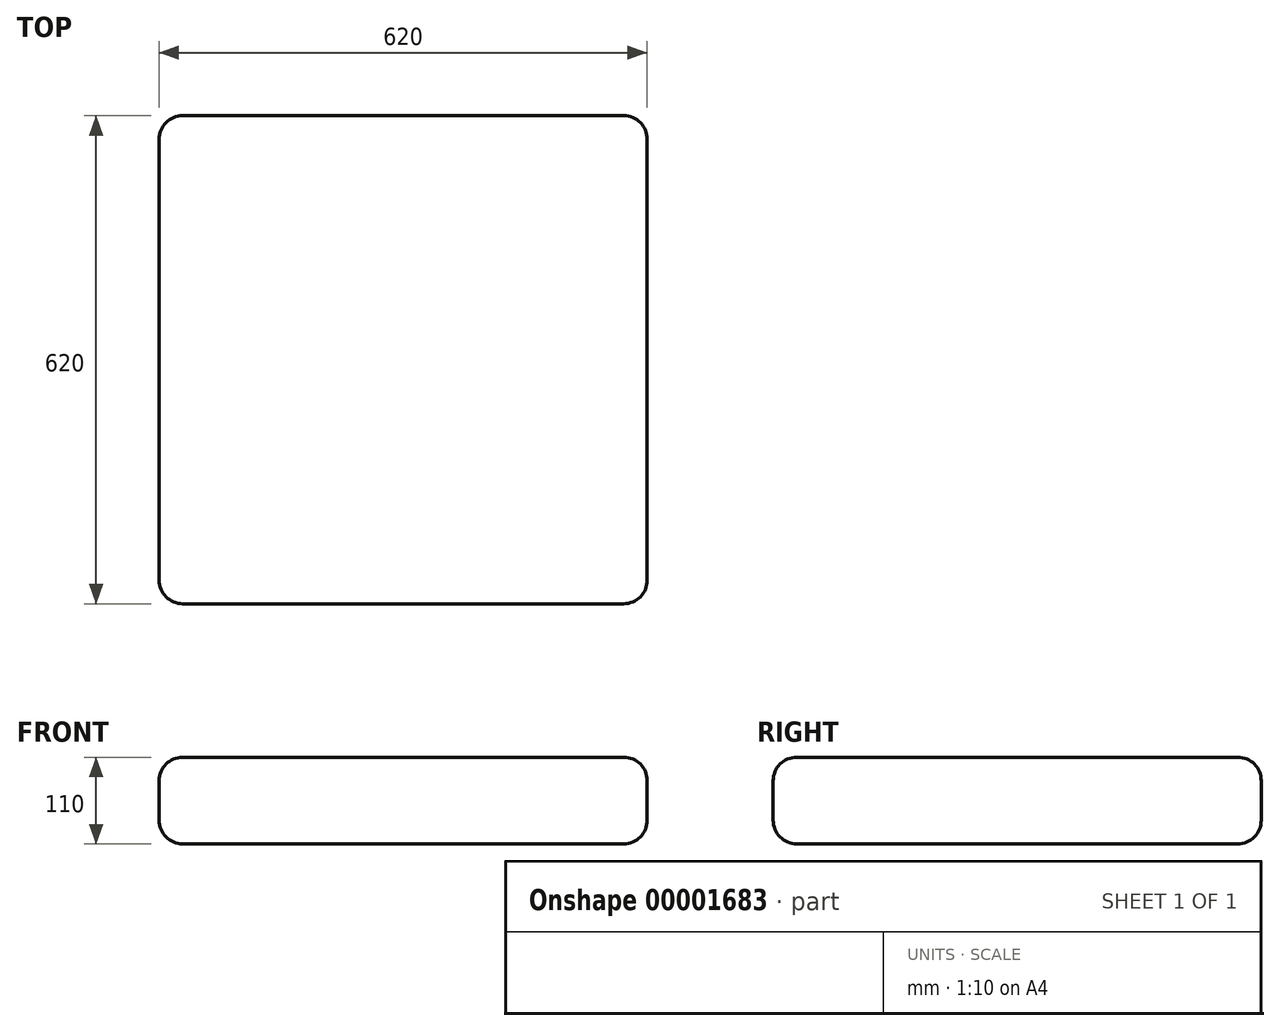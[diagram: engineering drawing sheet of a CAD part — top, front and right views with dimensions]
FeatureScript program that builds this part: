
annotation { "Feature Type Name" : "Feature", "Feature Type Description" : "" }
export const myFeature = defineFeature(function(context is Context, id is Id, definition is map)
    precondition{}
    {
        {
            var Q0;
            Q0=qCreatedBy(makeId("Top.planeOp"),FACE);
            var sketch = newSketch(context, id + "F0", { "sketchPlane" : qUnion([Q0])});
            skLineSegment(sketch, "E0.bottom", {"start": v(0, 0) * mm, "end": v(620, 0) * mm});
            skLineSegment(sketch, "E0.top", {"start": v(0, 620) * mm, "end": v(620, 620) * mm});
            skLineSegment(sketch, "E0.left", {"start": v(0, 0) * mm, "end": v(0, 620) * mm});
            skLineSegment(sketch, "E0.right", {"start": v(620, 0) * mm, "end": v(620, 620) * mm});
            skSolve(sketch);
        }
        {
            var Q0;
            Q0=makeQuery(id+"F0.imprint","IMPRINT",FACE,{"disambiguationData":[TD([[makeQuery(id+"F0.imprint","IMPRINT",EDGE,{"derivedFrom":sQuery(id+"F0.wireOp",EDGE,"E0.bottom")}),1.0]])]});
            extrude(context, id + "F1", {"entities" : qUnion([Q0]), "depth" : 110 * mm});
        }
        {
            var Q0;
            Q0=makeQuery(id+"F1.opExtrude","CAP_EDGE",EDGE,{"disambiguationData":[OSD([sQuery(id+"F0.wireOp",EDGE,"E0.bottom")])],"isStart":false});
            var Q1;
            Q1=makeQuery(id+"F1.opExtrude","CAP_EDGE",EDGE,{"disambiguationData":[OSD([sQuery(id+"F0.wireOp",EDGE,"E0.right")])],"isStart":false});
            var Q2;
            Q2=makeQuery(id+"F1.opExtrude","SWEPT_EDGE",EDGE,{"disambiguationData":[OSD([sQuery(id+"F0.wireOp",EDGE,"E0.bottom"),sQuery(id+"F0.wireOp",EDGE,"E0.right")])]});
            var Q3;
            Q3=makeQuery(id+"F1.opExtrude","SWEPT_EDGE",EDGE,{"disambiguationData":[OSD([sQuery(id+"F0.wireOp",EDGE,"E0.top"),sQuery(id+"F0.wireOp",EDGE,"E0.right")])]});
            var Q4;
            Q4=makeQuery(id+"F1.opExtrude","SWEPT_EDGE",EDGE,{"disambiguationData":[OSD([sQuery(id+"F0.wireOp",EDGE,"E0.bottom"),sQuery(id+"F0.wireOp",EDGE,"E0.left")])]});
            var Q5;
            Q5=makeQuery(id+"F1.opExtrude","CAP_EDGE",EDGE,{"disambiguationData":[OSD([sQuery(id+"F0.wireOp",EDGE,"E0.left")])],"isStart":false});
            var Q6;
            Q6=makeQuery(id+"F1.opExtrude","CAP_EDGE",EDGE,{"disambiguationData":[OSD([sQuery(id+"F0.wireOp",EDGE,"E0.left")])],"isStart":true});
            var Q7;
            Q7=makeQuery(id+"F1.opExtrude","CAP_EDGE",EDGE,{"disambiguationData":[OSD([sQuery(id+"F0.wireOp",EDGE,"E0.bottom")])],"isStart":true});
            var Q8;
            Q8=makeQuery(id+"F1.opExtrude","CAP_EDGE",EDGE,{"disambiguationData":[OSD([sQuery(id+"F0.wireOp",EDGE,"E0.right")])],"isStart":true});
            var Q9;
            Q9=makeQuery(id+"F1.opExtrude","CAP_EDGE",EDGE,{"disambiguationData":[OSD([sQuery(id+"F0.wireOp",EDGE,"E0.top")])],"isStart":true});
            var Q10;
            Q10=makeQuery(id+"F1.opExtrude","CAP_EDGE",EDGE,{"disambiguationData":[OSD([sQuery(id+"F0.wireOp",EDGE,"E0.top")])],"isStart":false});
            var Q11;
            Q11=makeQuery(id+"F1.opExtrude","SWEPT_EDGE",EDGE,{"disambiguationData":[OSD([sQuery(id+"F0.wireOp",EDGE,"E0.top"),sQuery(id+"F0.wireOp",EDGE,"E0.left")])]});
            fillet(context, id + "F2", {"entities" : qUnion([Q0, Q1, Q2, Q3, Q4, Q5, Q6, Q7, Q8, Q9, Q10, Q11]), "radius" : 30 * mm, "tangentPropagation" : true, "allowEdgeOverflow" : false});
        }
    });
